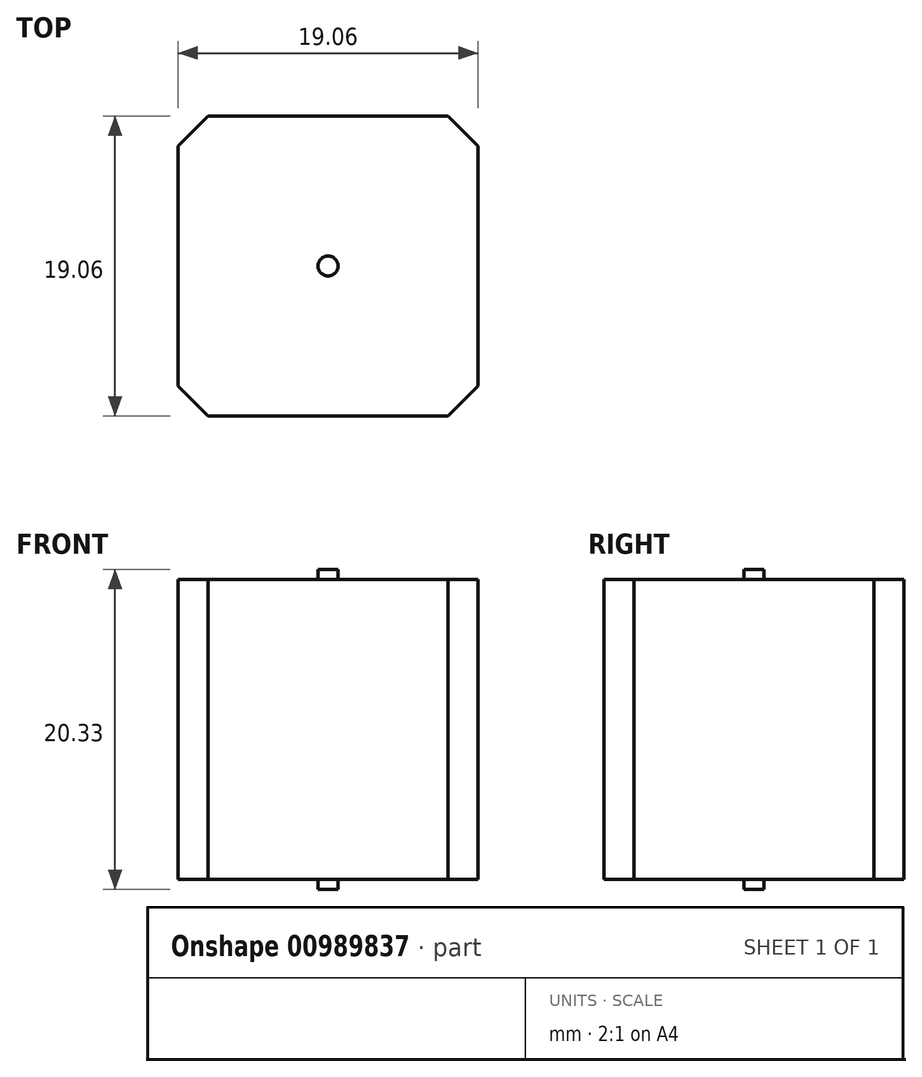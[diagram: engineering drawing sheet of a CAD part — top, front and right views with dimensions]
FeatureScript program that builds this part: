
annotation { "Feature Type Name" : "Feature", "Feature Type Description" : "" }
export const myFeature = defineFeature(function(context is Context, id is Id, definition is map)
    precondition{}
    {
        {
            var Q0;
            Q0=qCreatedBy(makeId("Top.planeOp"),FACE);
            var sketch = newSketch(context, id + "F0", { "sketchPlane" : qUnion([Q0])});
            skLineSegment(sketch, "E0.bottom", {"start": v(-9.53, 9.53) * mm, "end": v(9.53, 9.53) * mm});
            skLineSegment(sketch, "E0.top", {"start": v(-9.53, -9.53) * mm, "end": v(9.53, -9.53) * mm});
            skLineSegment(sketch, "E0.left", {"start": v(-9.53, 9.53) * mm, "end": v(-9.53, -9.53) * mm});
            skLineSegment(sketch, "E0.right", {"start": v(9.53, 9.53) * mm, "end": v(9.53, -9.53) * mm});
            skPoint(sketch, "E0.middle", {"position": v(0, 0) * mm});
            skSolve(sketch);
        }
        {
            var Q0;
            Q0=makeQuery(id+"F0.imprint","IMPRINT",FACE,{"disambiguationData":[TD([[makeQuery(id+"F0.imprint","IMPRINT",EDGE,{"derivedFrom":sQuery(id+"F0.wireOp",EDGE,"E0.bottom")}),-1.0]])]});
            extrude(context, id + "F1", {"entities" : qUnion([Q0]), "depth" : 19.05 * mm, "offsetDistance" : 25.4 * mm});
        }
        {
            var Q0;
            Q0=makeQuery(id+"F1.opExtrude","CAP_FACE",FACE,{"disambiguationData":[OSD([sQuery(id+"F0.wireOp",EDGE,"E0.bottom"),sQuery(id+"F0.wireOp",EDGE,"E0.top"),sQuery(id+"F0.wireOp",EDGE,"E0.left"),sQuery(id+"F0.wireOp",EDGE,"E0.right")])],"isStart":false});
            var sketch = newSketch(context, id + "F2", { "sketchPlane" : qUnion([Q0])});
            skLineSegment(sketch, "E1.0.0", {"start": v(-9.53, 9.53) * mm, "end": v(-9.53, -9.53) * mm});
            skLineSegment(sketch, "E1.0.1", {"start": v(-9.53, -9.53) * mm, "end": v(9.53, -9.53) * mm});
            skLineSegment(sketch, "E1.0.2", {"start": v(9.53, -9.53) * mm, "end": v(9.53, 9.53) * mm});
            skLineSegment(sketch, "E1.0.3", {"start": v(9.53, 9.53) * mm, "end": v(-9.53, 9.53) * mm});
            skCircle(sketch, "E2", {"center": v(0, 0) * mm, "radius": 0.64 * mm});
            skSolve(sketch);
        }
        {
            var Q0;
            Q0=makeQuery(id+"F2.imprint","IMPRINT",FACE,{"disambiguationData":[TD([[makeQuery(id+"F2.imprint","IMPRINT",EDGE,{"derivedFrom":sQuery(id+"F2.wireOp",EDGE,"E2")}),1.0]])]});
            extrude(context, id + "F3", {"entities" : qUnion([Q0]), "operationType" : NewBodyOperationType.ADD, "depth" : 0.64 * mm, "offsetDistance" : 25.4 * mm});
        }
        {
            var Q0;
            Q0=makeQuery(id+"F1.opExtrude","CAP_FACE",FACE,{"disambiguationData":[OSD([sQuery(id+"F0.wireOp",EDGE,"E0.bottom"),sQuery(id+"F0.wireOp",EDGE,"E0.top"),sQuery(id+"F0.wireOp",EDGE,"E0.left"),sQuery(id+"F0.wireOp",EDGE,"E0.right")])],"isStart":true});
            var sketch = newSketch(context, id + "F4", { "sketchPlane" : qUnion([Q0])});
            skCircle(sketch, "E3", {"center": v(0, 0) * mm, "radius": 0.64 * mm});
            skSolve(sketch);
        }
        {
            var Q0;
            Q0=makeQuery(id+"F4.imprint","IMPRINT",FACE,{"disambiguationData":[TD([[makeQuery(id+"F4.imprint","IMPRINT",EDGE,{"derivedFrom":sQuery(id+"F4.wireOp",EDGE,"E3")}),1.0]])]});
            extrude(context, id + "F5", {"entities" : qUnion([Q0]), "operationType" : NewBodyOperationType.ADD, "depth" : 0.64 * mm, "offsetDistance" : 25.4 * mm});
        }
        {
            var Q0;
            Q0=makeQuery(id+"F1.opExtrude","SWEPT_EDGE",EDGE,{"disambiguationData":[OSD([sQuery(id+"F0.wireOp",EDGE,"E0.top"),sQuery(id+"F0.wireOp",EDGE,"E0.left")])]});
            var Q1;
            Q1=makeQuery(id+"F1.opExtrude","SWEPT_EDGE",EDGE,{"disambiguationData":[OSD([sQuery(id+"F0.wireOp",EDGE,"E0.top"),sQuery(id+"F0.wireOp",EDGE,"E0.right")])]});
            var Q2;
            Q2=makeQuery(id+"F1.opExtrude","SWEPT_EDGE",EDGE,{"disambiguationData":[OSD([sQuery(id+"F0.wireOp",EDGE,"E0.bottom"),sQuery(id+"F0.wireOp",EDGE,"E0.right")])]});
            var Q3;
            Q3=makeQuery(id+"F1.opExtrude","SWEPT_EDGE",EDGE,{"disambiguationData":[OSD([sQuery(id+"F0.wireOp",EDGE,"E0.bottom"),sQuery(id+"F0.wireOp",EDGE,"E0.left")])]});
            chamfer(context, id + "F6", {"entities" : qUnion([Q0, Q1, Q2, Q3]), "width" : 1.9 * mm, "tangentPropagation" : true});
        }
    });
